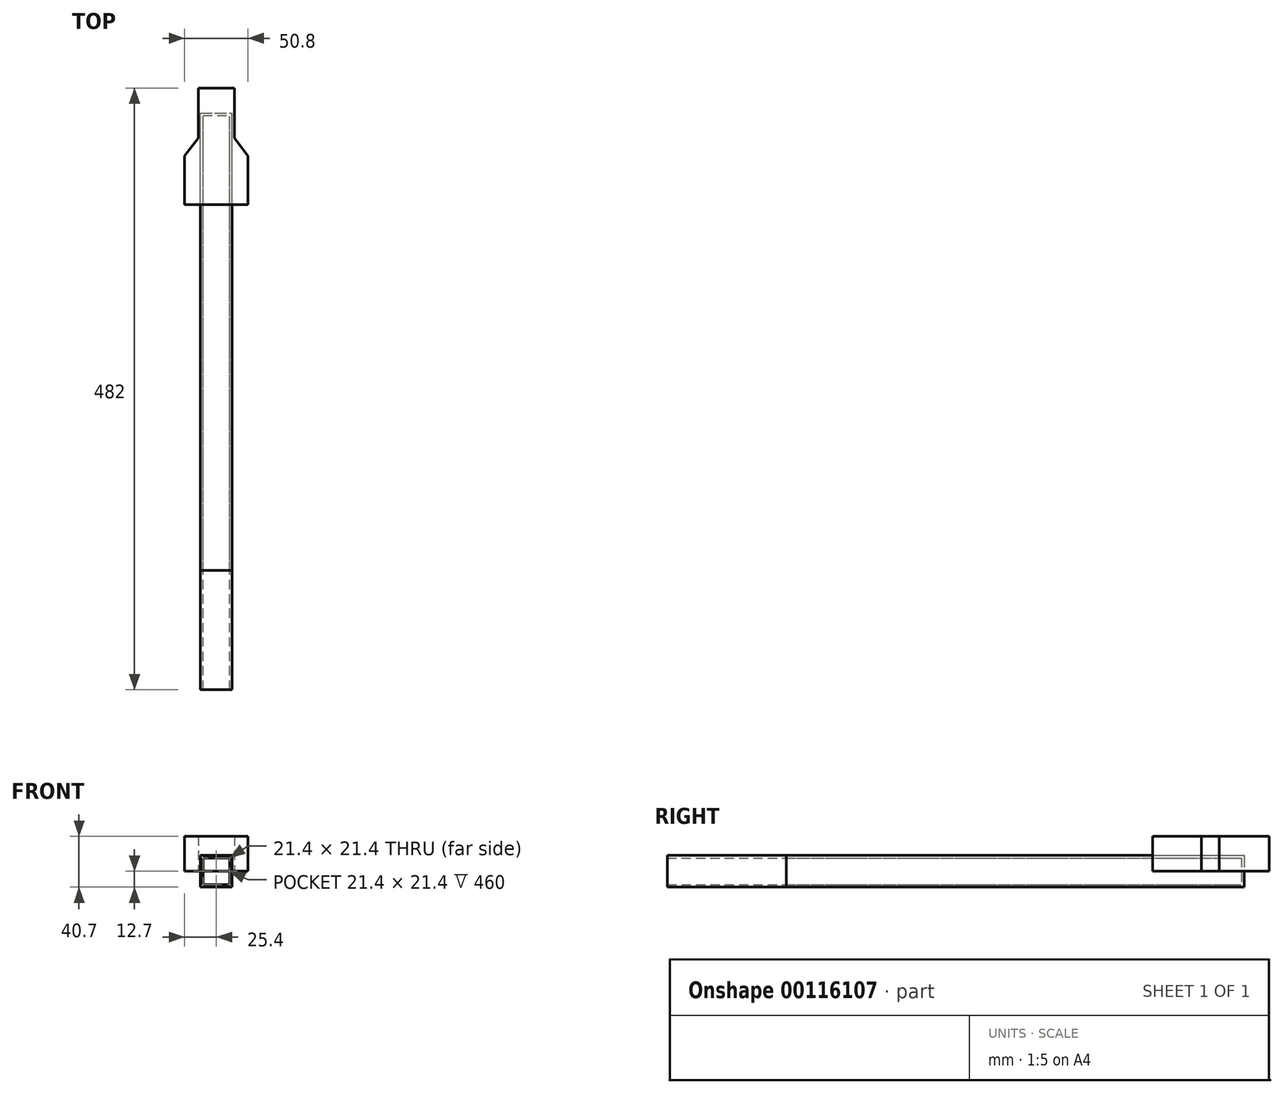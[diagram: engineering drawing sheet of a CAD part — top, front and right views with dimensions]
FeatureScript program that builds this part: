
annotation { "Feature Type Name" : "Feature", "Feature Type Description" : "" }
export const myFeature = defineFeature(function(context is Context, id is Id, definition is map)
    precondition{}
    {
        {
            var Q0;
            Q0=qCreatedBy(makeId("Front.planeOp"),FACE);
            var sketch = newSketch(context, id + "F0", { "sketchPlane" : qUnion([Q0])});
            skLineSegment(sketch, "E0.bottom", {"start": v(-12.7, 12.7) * mm, "end": v(12.7, 12.7) * mm});
            skLineSegment(sketch, "E0.top", {"start": v(-12.7, -12.7) * mm, "end": v(12.7, -12.7) * mm});
            skLineSegment(sketch, "E0.left", {"start": v(-12.7, 12.7) * mm, "end": v(-12.7, -12.7) * mm});
            skLineSegment(sketch, "E0.right", {"start": v(12.7, 12.7) * mm, "end": v(12.7, -12.7) * mm});
            skPoint(sketch, "E0.middle", {"position": v(0, 0) * mm});
            skSolve(sketch);
        }
        {
            var Q0;
            Q0=makeQuery(id+"F0.imprint","IMPRINT",FACE,{"disambiguationData":[TD([[makeQuery(id+"F0.imprint","IMPRINT",EDGE,{"derivedFrom":sQuery(id+"F0.wireOp",EDGE,"E0.bottom")}),-1.0]])]});
            extrude(context, id + "F1", {"entities" : qUnion([Q0]), "depth" : 462 * mm});
        }
        {
            var Q0;
            Q0=makeQuery(id+"F1.opExtrude","CAP_FACE",FACE,{"disambiguationData":[OSD([sQuery(id+"F0.wireOp",EDGE,"E0.bottom"),sQuery(id+"F0.wireOp",EDGE,"E0.top"),sQuery(id+"F0.wireOp",EDGE,"E0.left"),sQuery(id+"F0.wireOp",EDGE,"E0.right")])],"isStart":false});
            shell(context, id + "F2", {"entities" : qUnion([Q0]), "thickness" : 2 * mm});
        }
        {
            var Q0;
            Q0 = qSketchRegion(id + "F0", true);
            extrude(context, id + "F3", {"entities" : qUnion([Q0]), "depth" : 366.5 * mm});
        }
        {
            var Q0;
            Q0=makeQuery(id+"F3.opExtrude","CAP_FACE",FACE,{"disambiguationData":[OSD([sQuery(id+"F0.wireOp",EDGE,"E0.bottom"),sQuery(id+"F0.wireOp",EDGE,"E0.top"),sQuery(id+"F0.wireOp",EDGE,"E0.left"),sQuery(id+"F0.wireOp",EDGE,"E0.right")])],"isStart":false});
            var Q1;
            Q1=makeQuery(id+"F3.opExtrude","CAP_FACE",FACE,{"disambiguationData":[OSD([sQuery(id+"F0.wireOp",EDGE,"E0.bottom"),sQuery(id+"F0.wireOp",EDGE,"E0.top"),sQuery(id+"F0.wireOp",EDGE,"E0.left"),sQuery(id+"F0.wireOp",EDGE,"E0.right")])],"isStart":true});
            shell(context, id + "F4", {"entities" : qUnion([Q0, Q1]), "thickness" : 2 * mm});
        }
        {
            var Q0;
            Q0=qCreatedBy(makeId("Top.planeOp"),FACE);
            var sketch = newSketch(context, id + "F5", { "sketchPlane" : qUnion([Q0])});
            skLineSegment(sketch, "E1.bottom", {"start": v(-14.5, 20) * mm, "end": v(14.5, 20) * mm});
            skLineSegment(sketch, "E1.top", {"start": v(-14.5, -20) * mm, "end": v(14.5, -20) * mm});
            skLineSegment(sketch, "E1.left", {"start": v(-14.5, 20) * mm, "end": v(-14.5, -20) * mm});
            skLineSegment(sketch, "E1.right", {"start": v(14.5, 20) * mm, "end": v(14.5, -20) * mm});
            skPoint(sketch, "E1.middle", {"position": v(0, 0) * mm});
            skLineSegment(sketch, "E2", {"start": v(14.5, -20) * mm, "end": v(25.4, -34.32) * mm});
            skLineSegment(sketch, "E3", {"start": v(25.4, -34.32) * mm, "end": v(25.4, -73.39) * mm});
            skLineSegment(sketch, "E4", {"start": v(-14.5, -20) * mm, "end": v(-25.4, -34.32) * mm});
            skLineSegment(sketch, "E5", {"start": v(-25.4, -34.32) * mm, "end": v(-25.4, -73.39) * mm});
            skLineSegment(sketch, "E6", {"start": v(-25.4, -73.39) * mm, "end": v(25.4, -73.39) * mm});
            skSolve(sketch);
        }
        {
            var Q0;
            Q0 = qSketchRegion(id + "F5", true);
            extrude(context, id + "F6", {"entities" : qUnion([Q0]), "depth" : 28 * mm});
        }
    });
